# Revit family: Agta_Record_SldngDrset_THERMCORD-E-STA
name_source: partatom
category: Doors
revit_build: Autodesk Revit Architecture 2012 (Build: 20110916_2132(x64)
units: mm (PartAtom-declared; Revit-internal decimal feet)

## types (8) — shared parameters
AccessoryOptions = Contact manufacturer
AlternativeDoorsetGlazing = Part of glazing spec
AntiFingerTrapRequirement = Yes
Assembly Code = B2030110
BIMObjectName = THERMCORD E-STA.rfa
ClearHeightOfPassage = 2150 mm
Clearance Zones = No
Colour = Customer specific
Configuration = 1 or 2
Construction Type = Automatic Sliding Door
Description = Automatic Sliding Door
DistanceToWall = 63 mm  [stored 0.206693 ft]
DoorIncluded = Yes
DoorOpeningLeft = 1246 mm
DoorOpeningRight = 1246 mm
DoorsetFasteners = Screws
DoorsetOperation = Automatic
Drive Depth = 210 mm  [stored 0.688976 ft]
Drive Unit Center Distance = 1911 mm
Drive Unit Extra Width Left = 65 mm  [stored 0.213255 ft]
Drive Unit Extra Width Right = 65 mm  [stored 0.213255 ft]
DriveUnit = Sliding Door, Sheet Metal (Painted Steel)
ElectronicLock = Yes
Finish = Powder coated, Anodized, customer specific
FireExit = No
Floor List Depth = 89 mm  [stored 0.291995 ft]
FloorGuide = Sliding Door, Stainless Steel
FrameMaterial = Aluminium
FrameProfile = Aluminium
FrameSeal = Yes
Function = Exterior
GlassLayers = 2
GlassThickness1 = 8 mm (default)
GlassThickness2 = None (default)
GlassType = Part of glazing spec
HandicapAccessible = Yes
HasDrive = Yes
Inner Panel Width = 1246 mm
Interlacing profile 2 = No
Interlancing Profile Height = 2195 mm  [stored 7.20144 ft]
IsExternal = Yes
LeafColourOptions = All RAL, customer specific
Left Profile = No
Manufacturer = Record
ManufacturerName = Record
ManufacturerURL = www.agta-record.com
Material = Aluminium
Model = THERMCORD E-STA
ModelReference = Depends on the configuration
Mounting profile left = No
Mounting profile right = No
NBSDescription = Automatic Sliding Door
NBSReference = 25-50-20/175
OpeningWidth = 1200 mm
Outer Panel Width Left = 1213.18 mm  [stored 3.98025 ft]
Outer Panel Width Right = 1213.18 mm  [stored 3.98025 ft]
PanelFill = Sliding Door, Laminated Safety Glass (Clear)
PanelFrames = Sliding Door, Aluminium
PanelHeight = 2200 mm
ProductInformation = www.agta-record.com
ReferenceStandard = EN16005, EN16361, DIN 18650, etc.
ReplacementCost = Depends on the configuration and door type
Right Profile = No
SelfClosing = Yes
ServiceLifeDuration = 10-15 years
Shape = Rectangular
Side Panel Minimum Standard = 1246 mm
Side Panel Width Left = 1246 mm
Side Panel Width Right = 1246 mm
SmokeStop = No
SupportLength = 2497 mm
ThresholdRequired = Yes
ThresholdStripping = No additional required, part of the doorset
URL = www.agta-record.com
Uniclass2 = Ss_25_30_20_77
Version = Version 1.0
WallMountingProfile = No
WarrantyDescription = Depends on country
WarrantyDurationLabour = Depends on country
WarrantyDurationParts = Depends on country
WarrantyDurationUnit = Depends on country
WarrantyGuarantorLabour = Local door manufacturer
WarrantyGuarantorParts = Local door manufacturer
WarrantyStartDate = Depends on country
Weight = Depends on configuration and size
WithDriveCladding = Yes
WithinStandardSizes = Yes
WithoutDriveCladding(OnlyApplicableForTypesWithoutSidePanels) = No
zero-valued in all types: Cost, DoorOpening, DoorOpeningRestriction, ExtraLeft, ExtraRight, ExtraWidthLeft, ExtraWidthRight, NominalLength, Profile Opening Left, Profile Opening Right, ThermalTransmittance

## per-type parameters (varying)
| type | DoorSeal | DriveUnitHeight | Height | IfcExportAs | IfcExportType | Inner Panel Profile | Interlacing profile 1 | Interlacing profile 3 | Interlacing profile left | Interlacing profile right | Left Panel | Modified Profile | NominalHeight | NominalWidth | Right Panel | Rough Height | Rough Width | SupportLengthLeft | SupportLengthRight | TotalHeight | TotalWidth | Wall Opening Width | Width | Without side panels |
| THERMCORD E-STA-L 150mm drive unit height - left - with side panel | yes | 150 mm | 2300 mm |  |  | Yes | Yes | No | Yes | No | Yes | No | 2300 mm | 2497 mm | No | 2306 mm | 2503 mm | 1823 mm | 674 mm  [stored 2.21129 ft] | 2300 mm | 2497 mm | 2446 mm | 2497 mm | No |
| THERMCORD E-STA-R 150mm drive unit height - right - without side panels | 1 | 150 mm | 2300 mm |  |  | No | No | Yes | No | Yes | No | Yes | 2300 mm | 1305.5 mm | No | 2306 mm | 1311.5 mm | 674 mm  [stored 2.21129 ft] | 1823 mm | 2300 mm | 1305.5 mm | 1200 mm | 1305.5 mm | Yes |
| THERMCORD E-STA-R 150mm drive unit height - right - with side panel | 1 | 150 mm | 2300 mm |  |  | Yes | Yes | No | No | Yes | No | No | 2300 mm | 2497 mm | Yes | 2306 mm | 2503 mm | 674 mm  [stored 2.21129 ft] | 1823 mm | 2300 mm | 2497 mm | 2446 mm | 2497 mm | No |
| THERMCORD E-STA-L 150mm drive unit height - left - without side panels | 1 | 150 mm | 2300 mm |  |  | No | No | Yes | Yes | No | No | Yes | 2300 mm | 1305.5 mm | No | 2306 mm | 1311.5 mm | 1823 mm | 674 mm  [stored 2.21129 ft] | 2300 mm | 1305.5 mm | 1200 mm | 1305.5 mm | Yes |
| THERMCORD E-STA-L 200mm drive unit height - left - with side panel | 1 | 200 mm  [stored 0.656168 ft] | 2350 mm | IfcDoorStyle | Door | Yes | Yes | No | Yes | No | Yes | No | 2350 mm | 2497 mm | No | 2356 mm | 2503 mm | 1823 mm | 674 mm  [stored 2.21129 ft] | 2350 mm | 2497 mm | 2446 mm | 2497 mm | No |
| THERMCORD E-STA-L 200mm drive unit height - left - without side panels | 1 | 200 mm  [stored 0.656168 ft] | 2350 mm |  |  | No | No | Yes | Yes | No | No | Yes | 2350 mm | 1305.5 mm | No | 2356 mm | 1311.5 mm | 1823 mm | 674 mm  [stored 2.21129 ft] | 2350 mm | 1305.5 mm | 1200 mm | 1305.5 mm | Yes |
| THERMCORD E-STA-R 200mm drive unit height - right - with side panel | 1 | 150 mm | 2300 mm |  |  | Yes | Yes | No | No | Yes | No | No | 2300 mm | 2497 mm | Yes | 2306 mm | 2503 mm | 674 mm  [stored 2.21129 ft] | 1823 mm | 2300 mm | 2497 mm | 2446 mm | 2497 mm | No |
| THERMCORD E-STA-R 200mm drive unit height - right - without side panels | 1 | 200 mm  [stored 0.656168 ft] | 2350 mm |  |  | No | No | Yes | No | Yes | No | Yes | 2350 mm | 1305.5 mm | No | 2356 mm | 1311.5 mm | 674 mm  [stored 2.21129 ft] | 1823 mm | 2350 mm | 1305.5 mm | 1200 mm | 1305.5 mm | Yes |

note: [stored X ft] marks values corroborated as IEEE doubles in the binary element streams (Revit-internal decimal feet)

## geometry (parser evidence)
native form markers: Sweep x6
no freeform markers — native parametric forms only
